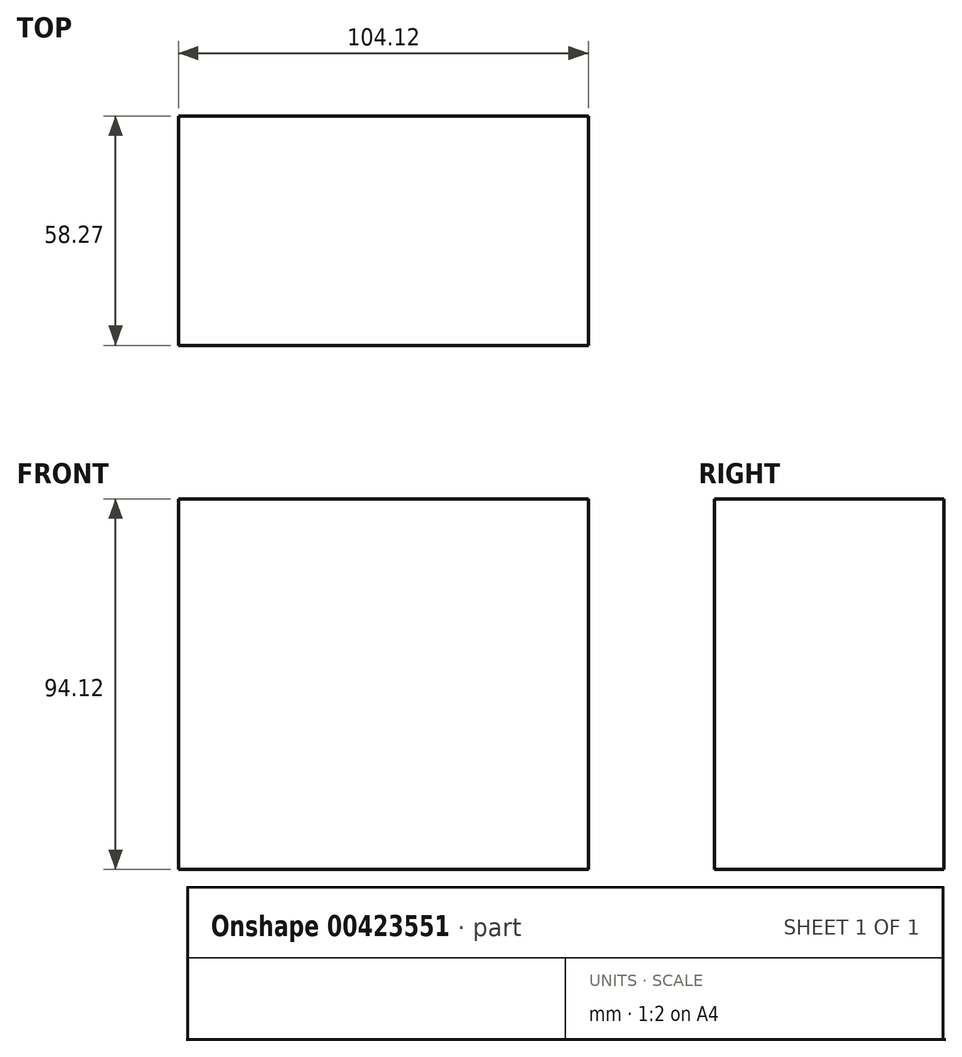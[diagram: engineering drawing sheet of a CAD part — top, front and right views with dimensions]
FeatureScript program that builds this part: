
annotation { "Feature Type Name" : "Feature", "Feature Type Description" : "" }
export const myFeature = defineFeature(function(context is Context, id is Id, definition is map)
    precondition{}
    {
        {
            var Q0;
            Q0=qCreatedBy(makeId("Front.planeOp"),FACE);
            var sketch = newSketch(context, id + "F0", { "sketchPlane" : qUnion([Q0])});
            skLineSegment(sketch, "E0.bottom", {"start": v(74.22, 0) * mm, "end": v(64.63, 0) * mm});
            skLineSegment(sketch, "E0.top", {"start": v(74.22, 0) * mm, "end": v(64.63, 0) * mm});
            skLineSegment(sketch, "E0.left", {"start": v(74.22, 0) * mm, "end": v(74.22, 0) * mm});
            skLineSegment(sketch, "E0.right", {"start": v(64.63, 0) * mm, "end": v(64.63, 0) * mm});
            skLineSegment(sketch, "E1.bottom", {"start": v(0, 30.58) * mm, "end": v(0, 30.58) * mm});
            skLineSegment(sketch, "E1.top", {"start": v(0, 17.24) * mm, "end": v(0, 17.24) * mm});
            skLineSegment(sketch, "E1.left", {"start": v(0, 30.58) * mm, "end": v(0, 17.24) * mm});
            skLineSegment(sketch, "E1.right", {"start": v(0, 30.58) * mm, "end": v(0, 17.24) * mm});
            skLineSegment(sketch, "E2.bottom", {"start": v(55.88, 56.49) * mm, "end": v(-48.24, 56.49) * mm});
            skLineSegment(sketch, "E2.top", {"start": v(55.88, -37.63) * mm, "end": v(-48.24, -37.63) * mm});
            skLineSegment(sketch, "E2.left", {"start": v(55.88, 56.49) * mm, "end": v(55.88, -37.63) * mm});
            skLineSegment(sketch, "E2.right", {"start": v(-48.24, 56.49) * mm, "end": v(-48.24, -37.63) * mm});
            skSolve(sketch);
        }
        {
            var Q0;
            Q0=makeQuery(id+"F0.imprint","IMPRINT",FACE,{"disambiguationData":[TD([[makeQuery(id+"F0.imprint","IMPRINT",EDGE,{"derivedFrom":sQuery(id+"F0.wireOp",EDGE,"E2.bottom")}),1.0]])]});
            extrude(context, id + "F1", {"entities" : qUnion([Q0]), "depth" : 58.27 * mm});
        }
    });
